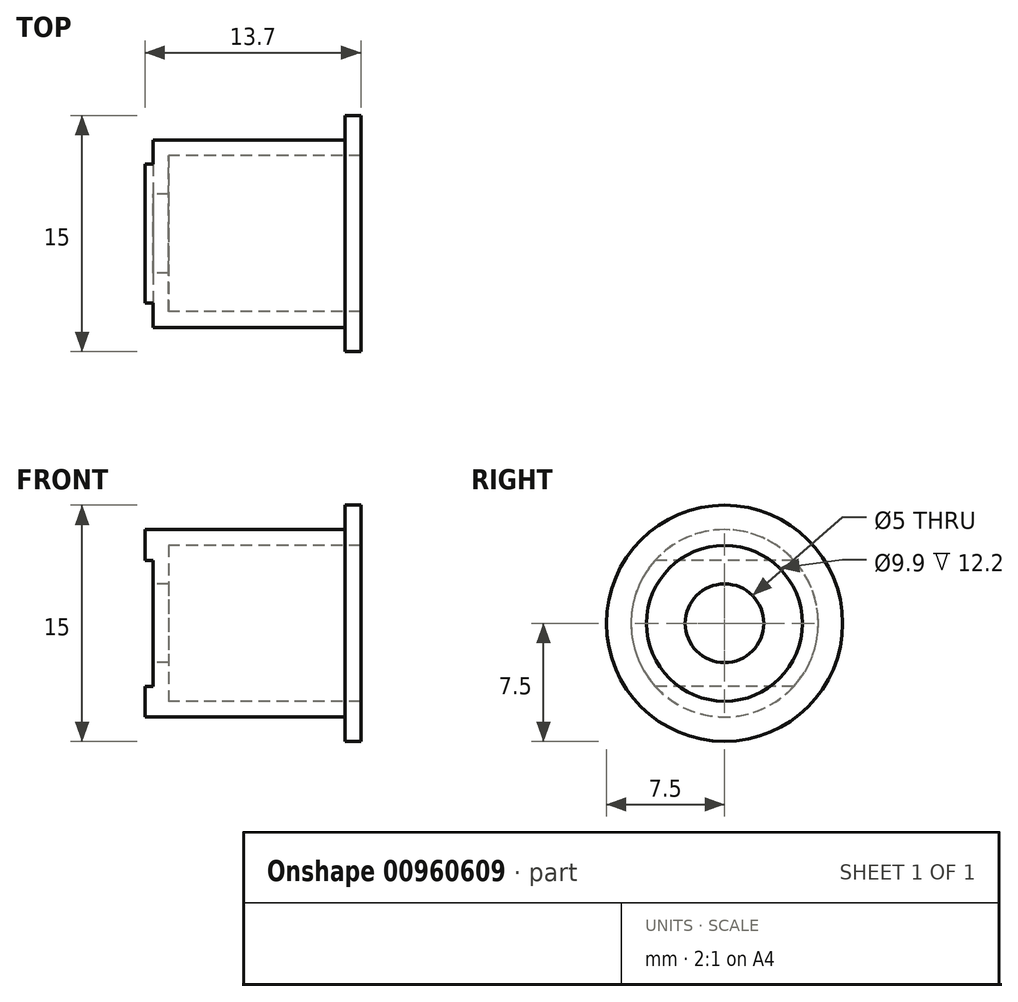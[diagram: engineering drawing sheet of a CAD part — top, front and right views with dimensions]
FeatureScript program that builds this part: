
annotation { "Feature Type Name" : "Feature", "Feature Type Description" : "" }
export const myFeature = defineFeature(function(context is Context, id is Id, definition is map)
    precondition{}
    {
        {
            var Q0;
            Q0=qCreatedBy(makeId("Front.planeOp"),FACE);
            var sketch = newSketch(context, id + "F0", { "sketchPlane" : qUnion([Q0])});
            skLineSegment(sketch, "E0", {"start": v(0, 2.5) * mm, "end": v(0, 5.95) * mm});
            skLineSegment(sketch, "E1", {"start": v(0, 5.95) * mm, "end": v(12.2, 5.95) * mm});
            skLineSegment(sketch, "E2", {"start": v(12.2, 5.95) * mm, "end": v(12.2, 7.5) * mm});
            skLineSegment(sketch, "E3", {"start": v(12.2, 7.5) * mm, "end": v(13.2, 7.5) * mm});
            skLineSegment(sketch, "E4", {"start": v(13.2, 7.5) * mm, "end": v(13.2, 4.95) * mm});
            skLineSegment(sketch, "E5", {"start": v(13.2, 4.95) * mm, "end": v(1, 4.95) * mm});
            skLineSegment(sketch, "E6", {"start": v(1, 4.95) * mm, "end": v(1, 2.5) * mm});
            skLineSegment(sketch, "E7", {"start": v(1, 2.5) * mm, "end": v(0, 2.5) * mm});
            skLineSegment(sketch, "E8", {"start": v(0, 0) * mm, "end": v(4.38, 0) * mm, "construction": true});
            skSolve(sketch);
        }
        {
            var Q0;
            Q0=makeQuery(id+"F0.imprint","IMPRINT",FACE,{"disambiguationData":[TD([[makeQuery(id+"F0.imprint","IMPRINT",EDGE,{"derivedFrom":sQuery(id+"F0.wireOp",EDGE,"E0")}),-1.0]])]});
            var Q1;
            Q1=sQuery(id+"F0.wireOp",EDGE,"E8");
            revolve(context, id + "F1", {"surfaceOperationType" : NewSurfaceOperationType.NEW, "entities" : qUnion([Q0]), "axis" : qUnion([Q1]), "revolveType" : RevolveType.FULL});
        }
        {
            var Q0;
            Q0=makeQuery(id+"F1.opRevolve","SWEPT_FACE",FACE,{"disambiguationData":[OSD([sQuery(id+"F0.wireOp",EDGE,"E0")])]});
            var sketch = newSketch(context, id + "F2", { "sketchPlane" : qUnion([Q0])});
            skLineSegment(sketch, "E9", {"start": v(-4.4, 4) * mm, "end": v(4.4, 4) * mm});
            skLineSegment(sketch, "E10", {"start": v(-4.4, -4) * mm, "end": v(4.4, -4) * mm});
            skSolve(sketch);
        }
        {
            var Q0;
            {var subQ0=sQuery(id+"F2.wireOp",EDGE,"E9");Q0=makeQuery(id+"F2.imprint","IMPRINT",FACE,{"disambiguationData":[TD([[makeQuery(id+"F2.imprint","IMPRINT",EDGE,{"derivedFrom":subQ0}),1.0]])]});}
            var Q1;
            {var subQ0=sQuery(id+"F2.wireOp",EDGE,"E10");Q1=makeQuery(id+"F2.imprint","IMPRINT",FACE,{"disambiguationData":[TD([[makeQuery(id+"F2.imprint","IMPRINT",EDGE,{"derivedFrom":subQ0}),-1.0]])]});}
            extrude(context, id + "F3", {"entities" : qUnion([Q0, Q1]), "operationType" : NewBodyOperationType.ADD, "depth" : .5 * mm, "offsetDistance" : 25 * mm});
        }
    });
